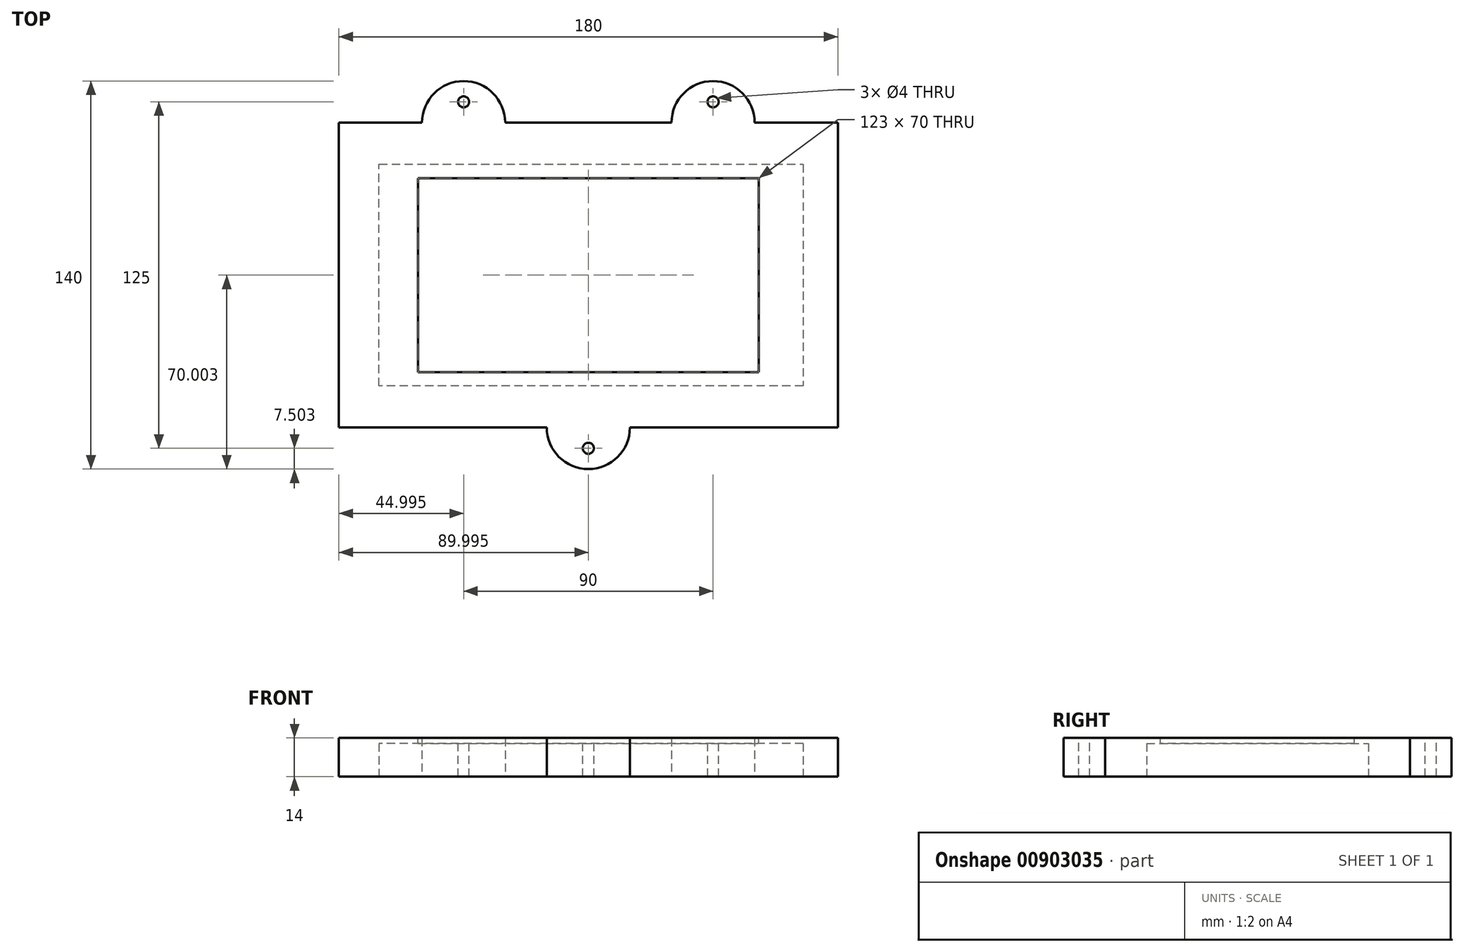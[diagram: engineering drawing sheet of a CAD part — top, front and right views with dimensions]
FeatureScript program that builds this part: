
annotation { "Feature Type Name" : "Feature", "Feature Type Description" : "" }
export const myFeature = defineFeature(function(context is Context, id is Id, definition is map)
    precondition{}
    {
        {
            var Q0;
            Q0=qCreatedBy(makeId("Top.planeOp"),FACE);
            var sketch = newSketch(context, id + "F0", { "sketchPlane" : qUnion([Q0])});
            skLineSegment(sketch, "E0.bottom", {"start": v(-81.43, 66.57) * mm, "end": v(-51.43, 66.57) * mm});
            skLineSegment(sketch, "E0.top", {"start": v(-81.43, -43.43) * mm, "end": v(-6.43, -43.43) * mm});
            skLineSegment(sketch, "E0.left", {"start": v(-81.43, 66.57) * mm, "end": v(-81.43, -43.43) * mm});
            skLineSegment(sketch, "E0.right", {"start": v(98.57, 66.57) * mm, "end": v(98.57, -43.43) * mm});
            skLineSegment(sketch, "E1", {"start": v(-81.43, 96.12) * mm, "end": v(8.57, 96.12) * mm, "construction": true});
            skPoint(sketch, "E1.endSnap0", {"position": v(8.57, 66.57) * mm});
            skLineSegment(sketch, "E2", {"start": v(8.57, 96.12) * mm, "end": v(98.57, 96.12) * mm, "construction": true});
            skLineSegment(sketch, "E3", {"start": v(-36.43, 81.57) * mm, "end": v(-36.43, 66.57) * mm, "construction": true});
            skLineSegment(sketch, "E4", {"start": v(53.57, 81.57) * mm, "end": v(53.57, 66.57) * mm, "construction": true});
            skArc(sketch, "E5", {"start": v(-21.43, 66.57) * mm, "mid": v(-36.43, 81.57) * mm, "end": v(-51.43, 66.57) * mm});
            skArc(sketch, "E6", {"start": v(68.57, 66.57) * mm, "mid": v(53.57, 81.57) * mm, "end": v(38.57, 66.57) * mm});
            skArc(sketch, "E7", {"start": v(-6.43, -43.43) * mm, "mid": v(8.57, -58.43) * mm, "end": v(23.57, -43.43) * mm});
            skLineSegment(sketch, "E8.trimOffspring", {"start": v(23.57, -43.43) * mm, "end": v(98.57, -43.43) * mm});
            skLineSegment(sketch, "E9.trimOffspring", {"start": v(-21.43, 66.57) * mm, "end": v(38.57, 66.57) * mm});
            skLineSegment(sketch, "E10.trimOffspring", {"start": v(68.57, 66.57) * mm, "end": v(98.57, 66.57) * mm});
            skPoint(sketch, "E11.orphan", {"position": v(53.57, 96.12) * mm});
            skPoint(sketch, "E12.orphan", {"position": v(-36.43, 96.12) * mm});
            skLineSegment(sketch, "E13", {"start": v(53.57, 74.07) * mm, "end": v(-36.43, 74.07) * mm, "construction": true});
            skLineSegment(sketch, "E14", {"start": v(8.57, -58.43) * mm, "end": v(8.57, -43.43) * mm, "construction": true});
            skCircle(sketch, "E15", {"center": v(8.57, -50.93) * mm, "radius": 2 * mm});
            skCircle(sketch, "E16", {"center": v(53.57, 74.07) * mm, "radius": 2 * mm});
            skCircle(sketch, "E17", {"center": v(-36.43, 74.07) * mm, "radius": 2 * mm});
            skSolve(sketch);
        }
        {
            var Q0;
            Q0=qSketchRegion(id+"F0",true);
            extrude(context, id + "F1", {"entities" : qUnion([Q0]), "depth" : 25 * mm, "offsetDistance" : 25 * mm});
        }
        {
            var Q0;
            Q0=makeQuery(id+"F1.opExtrude","SWEPT_FACE",FACE,{"disambiguationData":[OSD([sQuery(id+"F0.wireOp",EDGE,"E0.right")])]});
            var sketch = newSketch(context, id + "F2", { "sketchPlane" : qUnion([Q0])});
            skArc(sketch, "E18", {"start": v(22.82, 0) * mm, "mid": v(11.57, 11.25) * mm, "end": v(0.32, 0) * mm});
            skLineSegment(sketch, "E19", {"start": v(-64.9, 25) * mm, "end": v(-64.9, 15) * mm, "construction": true});
            skLineSegment(sketch, "E20", {"start": v(-64.9, 15) * mm, "end": v(92.3, 15) * mm, "construction": true});
            skArc(sketch, "E21", {"start": v(-20, 0) * mm, "mid": v(-41.23, 11.15) * mm, "end": v(-64.9, 15) * mm});
            skLineSegment(sketch, "E22", {"start": v(11.57, 0) * mm, "end": v(11.57, -67.92) * mm, "construction": true});
            skArc(sketch, "E23.MirrorCS", {"start": v(43.15, 0) * mm, "mid": v(64.38, 11.15) * mm, "end": v(88.05, 15) * mm});
            skLineSegment(sketch, "E24", {"start": v(88.05, 15) * mm, "end": v(88.05, -16.41) * mm});
            skLineSegment(sketch, "E25", {"start": v(88.05, -16.41) * mm, "end": v(-64.9, -16.41) * mm});
            skLineSegment(sketch, "E26", {"start": v(-64.9, -16.41) * mm, "end": v(-64.9, 15) * mm});
            skLineSegment(sketch, "E27", {"start": v(-20, 0) * mm, "end": v(0.32, 0) * mm});
            skLineSegment(sketch, "E28.MirrorCS", {"start": v(43.15, 0) * mm, "end": v(22.82, 0) * mm});
            skSolve(sketch);
        }
        {
            var Q0;
            Q0=qSketchRegion(id+"F2",true);
            extrude(context, id + "F3", {"entities" : qUnion([Q0]), "operationType" : NewBodyOperationType.REMOVE, "oppositeDirection" : true, "depth" : 276 * mm, "offsetDistance" : 25 * mm});
        }
        {
            var Q0;
            Q0=makeQuery(id+"F1.opExtrude","CAP_FACE",FACE,{"disambiguationData":[OSD([sQuery(id+"F0.wireOp",EDGE,"E0.bottom"),sQuery(id+"F0.wireOp",EDGE,"E0.top"),sQuery(id+"F0.wireOp",EDGE,"E0.left"),sQuery(id+"F0.wireOp",EDGE,"E0.right"),sQuery(id+"F0.wireOp",EDGE,"E5"),sQuery(id+"F0.wireOp",EDGE,"E6"),sQuery(id+"F0.wireOp",EDGE,"E7"),sQuery(id+"F0.wireOp",EDGE,"E8.trimOffspring"),sQuery(id+"F0.wireOp",EDGE,"E9.trimOffspring"),sQuery(id+"F0.wireOp",EDGE,"E10.trimOffspring"),sQuery(id+"F0.wireOp",EDGE,"E15"),sQuery(id+"F0.wireOp",EDGE,"E16"),sQuery(id+"F0.wireOp",EDGE,"E17")])],"isStart":false});
            var sketch = newSketch(context, id + "F4", { "sketchPlane" : qUnion([Q0])});
            skLineSegment(sketch, "E29", {"start": v(-66.43, 11.57) * mm, "end": v(83.57, 11.57) * mm, "construction": true});
            skPoint(sketch, "E30", {"position": v(63.57, 11.57) * mm});
            skPoint(sketch, "E31", {"position": v(-46.43, 11.57) * mm});
            skLineSegment(sketch, "E32", {"start": v(-66.43, 11.57) * mm, "end": v(-46.43, 11.57) * mm, "construction": true});
            skLineSegment(sketch, "E33", {"start": v(63.57, 11.57) * mm, "end": v(83.57, 11.57) * mm, "construction": true});
            skLineSegment(sketch, "E34", {"start": v(-56.43, 11.57) * mm, "end": v(-56.43, 22.87) * mm, "construction": true});
            skLineSegment(sketch, "E35", {"start": v(73.57, 11.57) * mm, "end": v(73.57, 22.87) * mm, "construction": true});
            skLineSegment(sketch, "E36", {"start": v(-56.43, 22.87) * mm, "end": v(-56.43, 42.87) * mm, "construction": true});
            skLineSegment(sketch, "E37", {"start": v(73.57, 22.87) * mm, "end": v(73.57, 42.87) * mm, "construction": true});
            skCircle(sketch, "E38", {"center": v(-56.43, 32.87) * mm, "radius": 2 * mm});
            skCircle(sketch, "E39", {"center": v(73.57, 32.87) * mm, "radius": 2 * mm});
            skLineSegment(sketch, "E40", {"start": v(-81.43, 11.57) * mm, "end": v(98.57, 11.57) * mm, "construction": true});
            skCircle(sketch, "E41.MirrorC", {"center": v(-56.43, -9.73) * mm, "radius": 2 * mm});
            skCircle(sketch, "E42.MirrorC", {"center": v(73.57, -9.73) * mm, "radius": 2 * mm});
            skPoint(sketch, "E43", {"position": v(8.57, 11.57) * mm});
            skSolve(sketch);
        }
        {
            var Q0;
            Q0=qSketchRegion(id+"F4",true);
            extrude(context, id + "F5", {"entities" : qUnion([Q0]), "operationType" : NewBodyOperationType.REMOVE, "oppositeDirection" : true, "depth" : 84.8 * mm, "offsetDistance" : 25 * mm});
        }
        {
            var Q0;
            Q0=makeQuery(id+"F1.opExtrude","CAP_FACE",FACE,{"disambiguationData":[OSD([sQuery(id+"F0.wireOp",EDGE,"E0.bottom"),sQuery(id+"F0.wireOp",EDGE,"E0.top"),sQuery(id+"F0.wireOp",EDGE,"E0.left"),sQuery(id+"F0.wireOp",EDGE,"E0.right"),sQuery(id+"F0.wireOp",EDGE,"E5"),sQuery(id+"F0.wireOp",EDGE,"E6"),sQuery(id+"F0.wireOp",EDGE,"E7"),sQuery(id+"F0.wireOp",EDGE,"E8.trimOffspring"),sQuery(id+"F0.wireOp",EDGE,"E9.trimOffspring"),sQuery(id+"F0.wireOp",EDGE,"E10.trimOffspring"),sQuery(id+"F0.wireOp",EDGE,"E15"),sQuery(id+"F0.wireOp",EDGE,"E16"),sQuery(id+"F0.wireOp",EDGE,"E17")])],"isStart":false});
            var sketch = newSketch(context, id + "F6", { "sketchPlane" : qUnion([Q0])});
            skCircle(sketch, "E44", {"center": v(-56.43, 32.87) * mm, "radius": 2.5 * mm});
            skCircle(sketch, "E45", {"center": v(73.57, 32.87) * mm, "radius": 2.5 * mm});
            skCircle(sketch, "E46", {"center": v(73.57, -9.73) * mm, "radius": 2.5 * mm});
            skCircle(sketch, "E47", {"center": v(-56.43, -9.73) * mm, "radius": 2.5 * mm});
            skSolve(sketch);
        }
        {
            var Q0;
            Q0=qSketchRegion(id+"F6",true);
            extrude(context, id + "F7", {"entities" : qUnion([Q0]), "operationType" : NewBodyOperationType.REMOVE, "oppositeDirection" : true, "depth" : 5 * mm, "offsetDistance" : 25 * mm});
        }
        {
            var Q0;
            Q0=makeQuery(id+"F1.opExtrude","CAP_FACE",FACE,{"disambiguationData":[OSD([sQuery(id+"F0.wireOp",EDGE,"E0.bottom"),sQuery(id+"F0.wireOp",EDGE,"E0.top"),sQuery(id+"F0.wireOp",EDGE,"E0.left"),sQuery(id+"F0.wireOp",EDGE,"E0.right"),sQuery(id+"F0.wireOp",EDGE,"E5"),sQuery(id+"F0.wireOp",EDGE,"E6"),sQuery(id+"F0.wireOp",EDGE,"E7"),sQuery(id+"F0.wireOp",EDGE,"E8.trimOffspring"),sQuery(id+"F0.wireOp",EDGE,"E9.trimOffspring"),sQuery(id+"F0.wireOp",EDGE,"E10.trimOffspring"),sQuery(id+"F0.wireOp",EDGE,"E15"),sQuery(id+"F0.wireOp",EDGE,"E16"),sQuery(id+"F0.wireOp",EDGE,"E17")])],"isStart":false});
            var sketch = newSketch(context, id + "F8", { "sketchPlane" : qUnion([Q0])});
            skLineSegment(sketch, "E48", {"start": v(-6.43, -43.43) * mm, "end": v(-81.43, -43.43) * mm});
            skLineSegment(sketch, "E49", {"start": v(-81.43, -43.43) * mm, "end": v(-81.43, 66.57) * mm});
            skLineSegment(sketch, "E50", {"start": v(-81.43, 66.57) * mm, "end": v(-51.43, 66.57) * mm});
            skLineSegment(sketch, "E51", {"start": v(-21.43, 66.57) * mm, "end": v(38.57, 66.57) * mm});
            skLineSegment(sketch, "E52", {"start": v(68.57, 66.57) * mm, "end": v(98.57, 66.57) * mm});
            skLineSegment(sketch, "E53", {"start": v(98.57, 66.57) * mm, "end": v(98.57, -43.43) * mm});
            skLineSegment(sketch, "E54", {"start": v(98.57, -43.43) * mm, "end": v(23.57, -43.43) * mm});
            skArc(sketch, "E55", {"start": v(68.57, 66.57) * mm, "mid": v(53.57, 81.57) * mm, "end": v(38.57, 66.57) * mm});
            skArc(sketch, "E56", {"start": v(-21.43, 66.57) * mm, "mid": v(-36.43, 81.57) * mm, "end": v(-51.43, 66.57) * mm});
            skArc(sketch, "E57", {"start": v(-6.43, -43.43) * mm, "mid": v(8.57, -58.43) * mm, "end": v(23.57, -43.43) * mm});
            skSolve(sketch);
        }
        {
            var Q0;
            Q0 = qSketchRegion(id + "F8", true);
            extrude(context, id + "F9", {"entities" : qUnion([Q0]), "depth" : 14 * mm, "offsetDistance" : 25 * mm});
        }
        {
            var Q0;
            Q0=makeQuery(id+"F1.opExtrude","SWEPT_BODY",BODY,{"disambiguationData":[OSD([sQuery(id+"F0.wireOp",EDGE,"E0.bottom"),sQuery(id+"F0.wireOp",EDGE,"E0.top"),sQuery(id+"F0.wireOp",EDGE,"E0.left"),sQuery(id+"F0.wireOp",EDGE,"E0.right"),sQuery(id+"F0.wireOp",EDGE,"E5"),sQuery(id+"F0.wireOp",EDGE,"E6"),sQuery(id+"F0.wireOp",EDGE,"E7"),sQuery(id+"F0.wireOp",EDGE,"E8.trimOffspring"),sQuery(id+"F0.wireOp",EDGE,"E9.trimOffspring"),sQuery(id+"F0.wireOp",EDGE,"E10.trimOffspring"),sQuery(id+"F0.wireOp",EDGE,"E15"),sQuery(id+"F0.wireOp",EDGE,"E16"),sQuery(id+"F0.wireOp",EDGE,"E17")])]});
            deleteBodies(context, id + "F10", {"entities" : qUnion([Q0])});
        }
        {
            var Q0;
            Q0=makeQuery(id+"F9.opExtrude","CAP_FACE",FACE,{"disambiguationData":[OSD([sQuery(id+"F8.wireOp",EDGE,"E48"),sQuery(id+"F8.wireOp",EDGE,"E49"),sQuery(id+"F8.wireOp",EDGE,"E50"),sQuery(id+"F8.wireOp",EDGE,"E51"),sQuery(id+"F8.wireOp",EDGE,"E52"),sQuery(id+"F8.wireOp",EDGE,"E53"),sQuery(id+"F8.wireOp",EDGE,"E54"),sQuery(id+"F8.wireOp",EDGE,"E55"),sQuery(id+"F8.wireOp",EDGE,"E56"),sQuery(id+"F8.wireOp",EDGE,"E57")])],"isStart":false});
            var sketch = newSketch(context, id + "F11", { "sketchPlane" : qUnion([Q0])});
            skLineSegment(sketch, "E58.bottom", {"start": v(-52.93, 46.57) * mm, "end": v(70.07, 46.57) * mm});
            skLineSegment(sketch, "E58.top", {"start": v(-52.93, -23.43) * mm, "end": v(70.07, -23.43) * mm});
            skLineSegment(sketch, "E58.left", {"start": v(-52.93, 46.57) * mm, "end": v(-52.93, -23.43) * mm});
            skLineSegment(sketch, "E58.right", {"start": v(70.07, 46.57) * mm, "end": v(70.07, -23.43) * mm});
            skPoint(sketch, "E59", {"position": v(8.57, 11.57) * mm});
            skPoint(sketch, "E59.positionSnap0", {"position": v(70.07, 11.57) * mm});
            skPoint(sketch, "E59.positionSnap1", {"position": v(8.57, 46.57) * mm});
            skPoint(sketch, "E60.positionSnap0", {"position": v(8.57, 66.57) * mm});
            skPoint(sketch, "E60.positionSnap1", {"position": v(-81.43, 11.57) * mm});
            skSolve(sketch);
        }
        {
            var Q0;
            Q0 = qSketchRegion(id + "F11", true);
            extrude(context, id + "F12", {"entities" : qUnion([Q0]), "operationType" : NewBodyOperationType.REMOVE, "oppositeDirection" : true, "depth" : 25 * mm, "offsetDistance" : 25 * mm});
        }
        {
            var Q0;
            Q0=makeQuery(id+"F9.opExtrude","CAP_FACE",FACE,{"disambiguationData":[OSD([sQuery(id+"F8.wireOp",EDGE,"E48"),sQuery(id+"F8.wireOp",EDGE,"E49"),sQuery(id+"F8.wireOp",EDGE,"E50"),sQuery(id+"F8.wireOp",EDGE,"E51"),sQuery(id+"F8.wireOp",EDGE,"E52"),sQuery(id+"F8.wireOp",EDGE,"E53"),sQuery(id+"F8.wireOp",EDGE,"E54"),sQuery(id+"F8.wireOp",EDGE,"E55"),sQuery(id+"F8.wireOp",EDGE,"E56"),sQuery(id+"F8.wireOp",EDGE,"E57")])],"isStart":true});
            var sketch = newSketch(context, id + "F13", { "sketchPlane" : qUnion([Q0])});
            skLineSegment(sketch, "E61", {"start": v(70.07, 23.43) * mm, "end": v(86.07, 23.43) * mm, "construction": true});
            skLineSegment(sketch, "E62", {"start": v(-52.93, 23.43) * mm, "end": v(-66.93, 23.43) * mm, "construction": true});
            skLineSegment(sketch, "E63", {"start": v(-52.93, 23.43) * mm, "end": v(-52.93, 28.43) * mm, "construction": true});
            skLineSegment(sketch, "E64", {"start": v(-52.93, -46.57) * mm, "end": v(-52.93, -51.57) * mm, "construction": true});
            skLineSegment(sketch, "E65", {"start": v(-66.93, 28.43) * mm, "end": v(-66.93, -51.57) * mm});
            skLineSegment(sketch, "E66", {"start": v(-66.93, -51.57) * mm, "end": v(86.07, -51.57) * mm});
            skLineSegment(sketch, "E67", {"start": v(86.07, -51.57) * mm, "end": v(86.07, 28.43) * mm});
            skLineSegment(sketch, "E68", {"start": v(86.07, 28.43) * mm, "end": v(-66.93, 28.43) * mm});
            skSolve(sketch);
        }
        {
            var Q0;
            Q0 = qSketchRegion(id + "F13", true);
            extrude(context, id + "F14", {"entities" : qUnion([Q0]), "operationType" : NewBodyOperationType.REMOVE, "oppositeDirection" : true, "depth" : 12 * mm, "offsetDistance" : 25 * mm});
        }
        {
            var Q0;
            Q0=makeQuery(id+"F9.opExtrude","CAP_FACE",FACE,{"disambiguationData":[OSD([sQuery(id+"F8.wireOp",EDGE,"E48"),sQuery(id+"F8.wireOp",EDGE,"E49"),sQuery(id+"F8.wireOp",EDGE,"E50"),sQuery(id+"F8.wireOp",EDGE,"E51"),sQuery(id+"F8.wireOp",EDGE,"E52"),sQuery(id+"F8.wireOp",EDGE,"E53"),sQuery(id+"F8.wireOp",EDGE,"E54"),sQuery(id+"F8.wireOp",EDGE,"E55"),sQuery(id+"F8.wireOp",EDGE,"E56"),sQuery(id+"F8.wireOp",EDGE,"E57")])],"isStart":false});
            var sketch = newSketch(context, id + "F15", { "sketchPlane" : qUnion([Q0])});
            skLineSegment(sketch, "E69", {"start": v(8.57, -43.43) * mm, "end": v(8.57, -58.43) * mm, "construction": true});
            skLineSegment(sketch, "E70", {"start": v(-36.43, 66.57) * mm, "end": v(-36.43, 81.57) * mm, "construction": true});
            skLineSegment(sketch, "E71", {"start": v(53.57, 66.57) * mm, "end": v(53.57, 81.57) * mm, "construction": true});
            skCircle(sketch, "E72", {"center": v(53.57, 74.07) * mm, "radius": 2 * mm});
            skCircle(sketch, "E73", {"center": v(-36.43, 74.07) * mm, "radius": 2 * mm});
            skCircle(sketch, "E74", {"center": v(8.57, -50.93) * mm, "radius": 2 * mm});
            skSolve(sketch);
        }
        {
            var Q0;
            Q0 = qSketchRegion(id + "F15", true);
            extrude(context, id + "F16", {"entities" : qUnion([Q0]), "operationType" : NewBodyOperationType.REMOVE, "oppositeDirection" : true, "depth" : 25 * mm, "offsetDistance" : 25 * mm});
        }
    });
